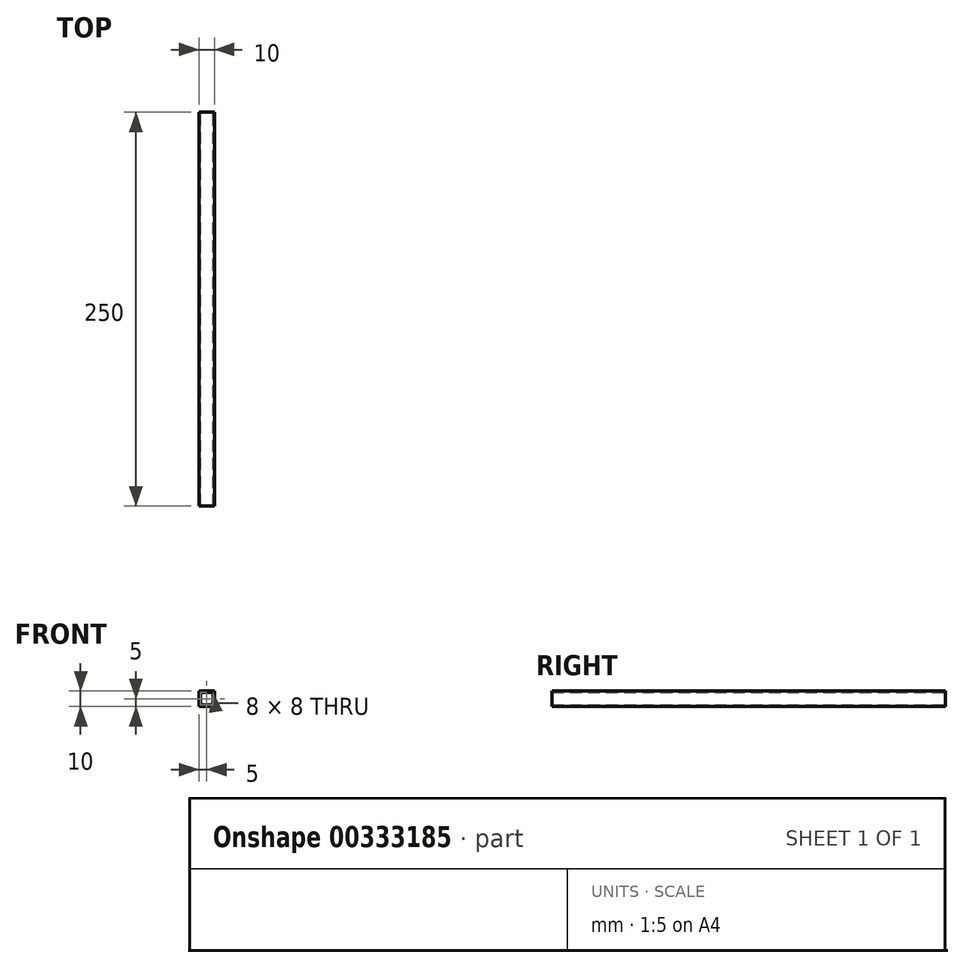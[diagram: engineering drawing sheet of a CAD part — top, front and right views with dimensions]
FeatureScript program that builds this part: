
annotation { "Feature Type Name" : "Feature", "Feature Type Description" : "" }
export const myFeature = defineFeature(function(context is Context, id is Id, definition is map)
    precondition{}
    {
        {
            var Q0;
            Q0=qCreatedBy(makeId("Front.planeOp"),FACE);
            var sketch = newSketch(context, id + "F0", { "sketchPlane" : qUnion([Q0])});
            skLineSegment(sketch, "E0.bottom", {"start": v(5, -5) * mm, "end": v(-5, -5) * mm});
            skLineSegment(sketch, "E0.top", {"start": v(5, 5) * mm, "end": v(-5, 5) * mm});
            skLineSegment(sketch, "E0.left", {"start": v(5, -5) * mm, "end": v(5, 5) * mm});
            skLineSegment(sketch, "E0.right", {"start": v(-5, -5) * mm, "end": v(-5, 5) * mm});
            skPoint(sketch, "E0.middle", {"position": v(0, 0) * mm});
            skLineSegment(sketch, "E1.bottom", {"start": v(4, -4) * mm, "end": v(-4, -4) * mm});
            skLineSegment(sketch, "E1.top", {"start": v(4, 4) * mm, "end": v(-4, 4) * mm});
            skLineSegment(sketch, "E1.left", {"start": v(4, -4) * mm, "end": v(4, 4) * mm});
            skLineSegment(sketch, "E1.right", {"start": v(-4, -4) * mm, "end": v(-4, 4) * mm});
            skSolve(sketch);
        }
        {
            var Q0;
            Q0=qSketchRegion(id+"F0",true);
            extrude(context, id + "F1", {"entities" : qUnion([Q0]), "endBound" : BoundingType.SYMMETRIC, "depth" : 250 * mm});
        }
    });
